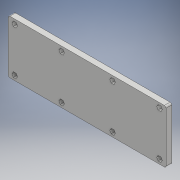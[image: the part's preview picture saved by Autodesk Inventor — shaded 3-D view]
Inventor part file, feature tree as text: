
AUTODESK INVENTOR PART (.ipt)
format: ipt  version: 2017 SP1 (Build 210196100, 196)  size: 211,968 bytes
history: native  units: mm
features: extrude x3, mirror x3, sketch x3, fillet x2, pattern_linear x1, shell x1, thicken_offset x1
ambient origin geometry x8: Origin, YZ Plane, XZ Plane, XY Plane, X Axis, Y Axis, Z Axis, Center Point
bodies: Solid1 (feature_tree)
feature tree (14):
  extrude  "Extrusion1"  Depth=66.0mm
  fillet  "Fillet1"  Radius=7.0mm
  extrude  "Extrusion2"  Depth=2.0mm
  mirror  "Mirror1"
  extrude  "Extrusion3"  Depth=5.0mm
  pattern_linear  "Rectangular Pattern1"  Spacing1=2.0mm  [1 undecoded]
  mirror  "Mirror2"
  mirror  "Mirror3"
  shell  "Shell1"  Thickness=1.0mm
  thicken_offset  "Thicken1"
  fillet  "Fillet2"  Radius=3.2mm
  sketch  "Sketch1"  dims[d0=195.0mm d1=66.0mm d2=7.0mm d3=0.0mm]
  sketch  "Sketch2"  dims[d4=2.0mm d5=2.0mm]
  sketch  "Sketch3"  dims[d6=1.0mm d7=1.0mm d8=2.0mm d9=1.0mm d10=3.2mm d11=3.2mm d12=1.0mm d13=3.2mm d14=1.0mm d15=3.2mm d16=58.0mm d17=63.0mm d18=58.0mm d19=5.75mm d21=8.0mm d22=7.0mm d23=0.0mm d24=3.0mm d25=5.0mm d26=0.0mm d27=20.0mm d29=58.0mm]
note: 1 required parameter value undecoded (feature->parameter linkage not recoverable at this tier; creation-order binding heuristic only, values carry confidence <= 0.55)
